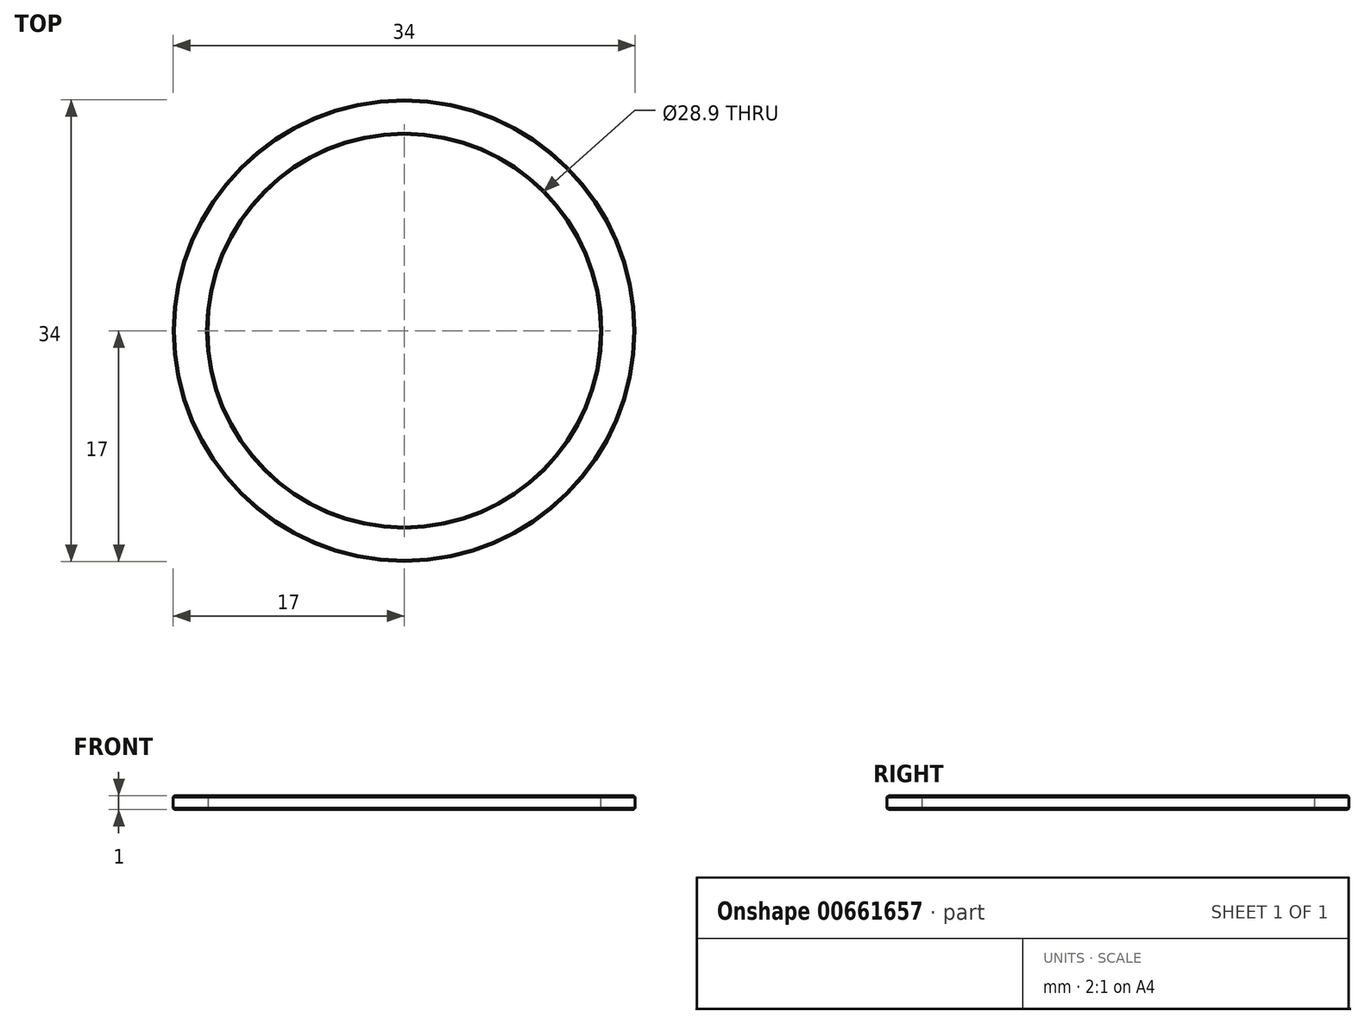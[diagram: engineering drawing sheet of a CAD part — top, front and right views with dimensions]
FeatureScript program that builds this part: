
annotation { "Feature Type Name" : "Feature", "Feature Type Description" : "" }
export const myFeature = defineFeature(function(context is Context, id is Id, definition is map)
    precondition{}
    {
        {
            var Q0;
            Q0=qCreatedBy(makeId("Top.planeOp"),FACE);
            var sketch = newSketch(context, id + "F0", { "sketchPlane" : qUnion([Q0])});
            skCircle(sketch, "E0", {"center": v(0, 0) * mm, "radius": 14.45 * mm});
            skCircle(sketch, "E1", {"center": v(0, 0) * mm, "radius": 17 * mm});
            skCircle(sketch, "E2", {"center": v(0, 0) * mm, "radius": 16 * mm});
            skSolve(sketch);
        }
        {
            var Q0;
            Q0=makeQuery(id+"F0.imprint","IMPRINT",FACE,{"disambiguationData":[TD([[makeQuery(id+"F0.imprint","IMPRINT",EDGE,{"derivedFrom":sQuery(id+"F0.wireOp",EDGE,"E0")}),-1.0]])]});
            var Q1;
            Q1=makeQuery(id+"F0.imprint","IMPRINT",FACE,{"disambiguationData":[TD([[makeQuery(id+"F0.imprint","IMPRINT",EDGE,{"derivedFrom":sQuery(id+"F0.wireOp",EDGE,"E1")}),1.0]])]});
            extrude(context, id + "F1", {"entities" : qUnion([Q0, Q1]), "endBound" : BoundingType.SYMMETRIC, "depth" : 1 * mm, "offsetDistance" : 25 * mm});
        }
        {
            var Q0;
            Q0=makeQuery(id+"F1.opExtrude","CAP_EDGE",EDGE,{"disambiguationData":[OSD([sQuery(id+"F0.wireOp",EDGE,"E1")])],"isStart":false});
            var Q1;
            Q1=makeQuery(id+"F1.opExtrude","CAP_EDGE",EDGE,{"disambiguationData":[OSD([sQuery(id+"F0.wireOp",EDGE,"E1")])],"isStart":true});
            chamfer(context, id + "F2", {"entities" : qUnion([Q0, Q1]), "width" : 0.1 * mm, "tangentPropagation" : true});
        }
        {
            var Q0;
            Q0=makeQuery(id+"F1.opExtrude","CAP_FACE",FACE,{"disambiguationData":[OSD([sQuery(id+"F0.wireOp",EDGE,"E0"),sQuery(id+"F0.wireOp",EDGE,"E1")])],"isStart":false});
            var sketch = newSketch(context, id + "F3", { "sketchPlane" : qUnion([Q0])});
            skPoint(sketch, "E3.0", {"position": v(0, 0) * mm});
            skCircle(sketch, "E4.0", {"center": v(0, 0) * mm, "radius": 14.45 * mm});
            skCircle(sketch, "E5.0", {"center": v(0, 0) * mm, "radius": 17 * mm});
            skCircle(sketch, "E6", {"center": v(0, 0) * mm, "radius": 14.97 * mm, "construction": true});
            skCircle(sketch, "E7.0", {"center": v(0, 0) * mm, "radius": 16.9 * mm});
            skCircle(sketch, "E8.cCircle", {"center": v(0, 0) * mm, "radius": 14.95 * mm, "construction": true});
            skLineSegment(sketch, "E8.0", {"start": v(-3.72, -14.5) * mm, "end": v(-5.51, -13.92) * mm});
            skLineSegment(sketch, "E8.1", {"start": v(-5.51, -13.92) * mm, "end": v(-7.21, -13.12) * mm});
            skLineSegment(sketch, "E8.2", {"start": v(-7.21, -13.12) * mm, "end": v(-8.8, -12.12) * mm});
            skLineSegment(sketch, "E8.3", {"start": v(-8.8, -12.12) * mm, "end": v(-10.25, -10.92) * mm});
            skLineSegment(sketch, "E8.4", {"start": v(-10.25, -10.92) * mm, "end": v(-11.54, -9.55) * mm});
            skLineSegment(sketch, "E8.5", {"start": v(-11.54, -9.55) * mm, "end": v(-12.64, -8.02) * mm});
            skLineSegment(sketch, "E8.6", {"start": v(-12.64, -8.02) * mm, "end": v(-13.55, -6.38) * mm});
            skLineSegment(sketch, "E8.7", {"start": v(-13.55, -6.38) * mm, "end": v(-14.24, -4.63) * mm});
            skLineSegment(sketch, "E8.8", {"start": v(-14.24, -4.63) * mm, "end": v(-14.7, -2.8) * mm});
            skLineSegment(sketch, "E8.9", {"start": v(-14.7, -2.8) * mm, "end": v(-14.95, -0.94) * mm});
            skLineSegment(sketch, "E8.10", {"start": v(-14.95, -0.94) * mm, "end": v(-14.95, 0.94) * mm});
            skLineSegment(sketch, "E8.11", {"start": v(-14.95, 0.94) * mm, "end": v(-14.7, 2.8) * mm});
            skLineSegment(sketch, "E8.12", {"start": v(-14.7, 2.8) * mm, "end": v(-14.24, 4.63) * mm});
            skLineSegment(sketch, "E8.13", {"start": v(-14.24, 4.63) * mm, "end": v(-13.55, 6.38) * mm});
            skLineSegment(sketch, "E8.14", {"start": v(-13.55, 6.38) * mm, "end": v(-12.64, 8.02) * mm});
            skLineSegment(sketch, "E8.15", {"start": v(-12.64, 8.02) * mm, "end": v(-11.54, 9.55) * mm});
            skLineSegment(sketch, "E8.16", {"start": v(-11.54, 9.55) * mm, "end": v(-10.25, 10.92) * mm});
            skLineSegment(sketch, "E8.17", {"start": v(-10.25, 10.92) * mm, "end": v(-8.8, 12.12) * mm});
            skLineSegment(sketch, "E8.18", {"start": v(-8.8, 12.12) * mm, "end": v(-7.21, 13.12) * mm});
            skLineSegment(sketch, "E8.19", {"start": v(-7.21, 13.12) * mm, "end": v(-5.51, 13.92) * mm});
            skLineSegment(sketch, "E8.20", {"start": v(-5.51, 13.92) * mm, "end": v(-3.72, 14.5) * mm});
            skLineSegment(sketch, "E8.21", {"start": v(-3.72, 14.5) * mm, "end": v(-1.88, 14.86) * mm});
            skLineSegment(sketch, "E8.22", {"start": v(-1.88, 14.86) * mm, "end": v(0, 14.97) * mm});
            skLineSegment(sketch, "E8.23", {"start": v(0, 14.97) * mm, "end": v(1.88, 14.86) * mm});
            skLineSegment(sketch, "E8.24", {"start": v(1.88, 14.86) * mm, "end": v(3.72, 14.5) * mm});
            skLineSegment(sketch, "E8.25", {"start": v(3.72, 14.5) * mm, "end": v(5.51, 13.92) * mm});
            skLineSegment(sketch, "E8.26", {"start": v(5.51, 13.92) * mm, "end": v(7.21, 13.12) * mm});
            skLineSegment(sketch, "E8.27", {"start": v(7.21, 13.12) * mm, "end": v(8.8, 12.12) * mm});
            skLineSegment(sketch, "E8.28", {"start": v(8.8, 12.12) * mm, "end": v(10.25, 10.92) * mm});
            skLineSegment(sketch, "E8.29", {"start": v(10.25, 10.92) * mm, "end": v(11.54, 9.55) * mm});
            skLineSegment(sketch, "E8.30", {"start": v(11.54, 9.55) * mm, "end": v(12.64, 8.02) * mm});
            skLineSegment(sketch, "E8.31", {"start": v(12.64, 8.02) * mm, "end": v(13.55, 6.38) * mm});
            skLineSegment(sketch, "E8.32", {"start": v(13.55, 6.38) * mm, "end": v(14.24, 4.63) * mm});
            skLineSegment(sketch, "E8.33", {"start": v(14.24, 4.63) * mm, "end": v(14.7, 2.8) * mm});
            skLineSegment(sketch, "E8.34", {"start": v(14.7, 2.8) * mm, "end": v(14.95, 0.94) * mm});
            skLineSegment(sketch, "E8.35", {"start": v(14.95, 0.94) * mm, "end": v(14.95, -0.94) * mm});
            skLineSegment(sketch, "E8.36", {"start": v(14.95, -0.94) * mm, "end": v(14.7, -2.8) * mm});
            skLineSegment(sketch, "E8.37", {"start": v(14.7, -2.8) * mm, "end": v(14.24, -4.63) * mm});
            skLineSegment(sketch, "E8.38", {"start": v(14.24, -4.63) * mm, "end": v(13.55, -6.38) * mm});
            skLineSegment(sketch, "E8.39", {"start": v(13.55, -6.38) * mm, "end": v(12.64, -8.02) * mm});
            skLineSegment(sketch, "E8.40", {"start": v(12.64, -8.02) * mm, "end": v(11.54, -9.55) * mm});
            skLineSegment(sketch, "E8.41", {"start": v(11.54, -9.55) * mm, "end": v(10.25, -10.92) * mm});
            skLineSegment(sketch, "E8.42", {"start": v(10.25, -10.92) * mm, "end": v(8.8, -12.12) * mm});
            skLineSegment(sketch, "E8.43", {"start": v(8.8, -12.12) * mm, "end": v(7.21, -13.12) * mm});
            skLineSegment(sketch, "E8.44", {"start": v(7.21, -13.12) * mm, "end": v(5.51, -13.92) * mm});
            skLineSegment(sketch, "E8.45", {"start": v(5.51, -13.92) * mm, "end": v(3.72, -14.5) * mm});
            skLineSegment(sketch, "E8.46", {"start": v(3.72, -14.5) * mm, "end": v(1.88, -14.86) * mm});
            skLineSegment(sketch, "E8.47", {"start": v(1.88, -14.86) * mm, "end": v(0, -14.97) * mm});
            skLineSegment(sketch, "E8.48", {"start": v(0, -14.97) * mm, "end": v(-1.88, -14.86) * mm});
            skLineSegment(sketch, "E8.49", {"start": v(-1.88, -14.86) * mm, "end": v(-3.72, -14.5) * mm});
            skPoint(sketch, "E8.0.midPoint", {"position": v(-4.62, -14.21) * mm});
            skLineSegment(sketch, "E9", {"start": v(0, 0) * mm, "end": v(0, 14.97) * mm, "construction": true});
            skLineSegment(sketch, "E10", {"start": v(0, 0) * mm, "end": v(1.88, 14.86) * mm, "construction": true});
            skLineSegment(sketch, "E11", {"start": v(0, 0) * mm, "end": v(3.72, 14.5) * mm, "construction": true});
            skText(sketch, "E12", { "text": "7", "fontName": "OpenSans-Regular.ttf"});
            skText(sketch, "E13", { "text": "8", "fontName": "OpenSans-Regular.ttf"});
            skText(sketch, "E14", { "text": "6", "fontName": "OpenSans-Regular.ttf"});
            skLineSegment(sketch, "E15", {"start": v(0, 0) * mm, "end": v(7.21, 13.12) * mm, "construction": true});
            skText(sketch, "E16", { "text": "C", "fontName": "OpenSans-Regular.ttf"});
            const initialGuessF3  = {"E12": [-0.00061, 0.01497, 1, 0, 0.0015], "E13": [0.00313, 0.01466, 0.96858, -0.24869, 0.0015], "E14": [0.00127, 0.01493, 0.99211, -0.12533, 0.0015], "E16": [0.0066, 0.01346, 0.8763, -0.48175, 0.0015]};
            skSetInitialGuess(sketch, initialGuessF3);
            skSolve(sketch);
        }
        {
            var Q0;
            Q0=makeQuery(id+"F1.opExtrude","CAP_EDGE",EDGE,{"disambiguationData":[OSD([sQuery(id+"F0.wireOp",EDGE,"E0")])],"isStart":false});
            var Q1;
            Q1=makeQuery(id+"F1.opExtrude","CAP_EDGE",EDGE,{"disambiguationData":[OSD([sQuery(id+"F0.wireOp",EDGE,"E0")])],"isStart":true});
            chamfer(context, id + "F4", {"entities" : qUnion([Q0, Q1]), "width" : 0.1 * mm, "tangentPropagation" : true});
        }
    });
